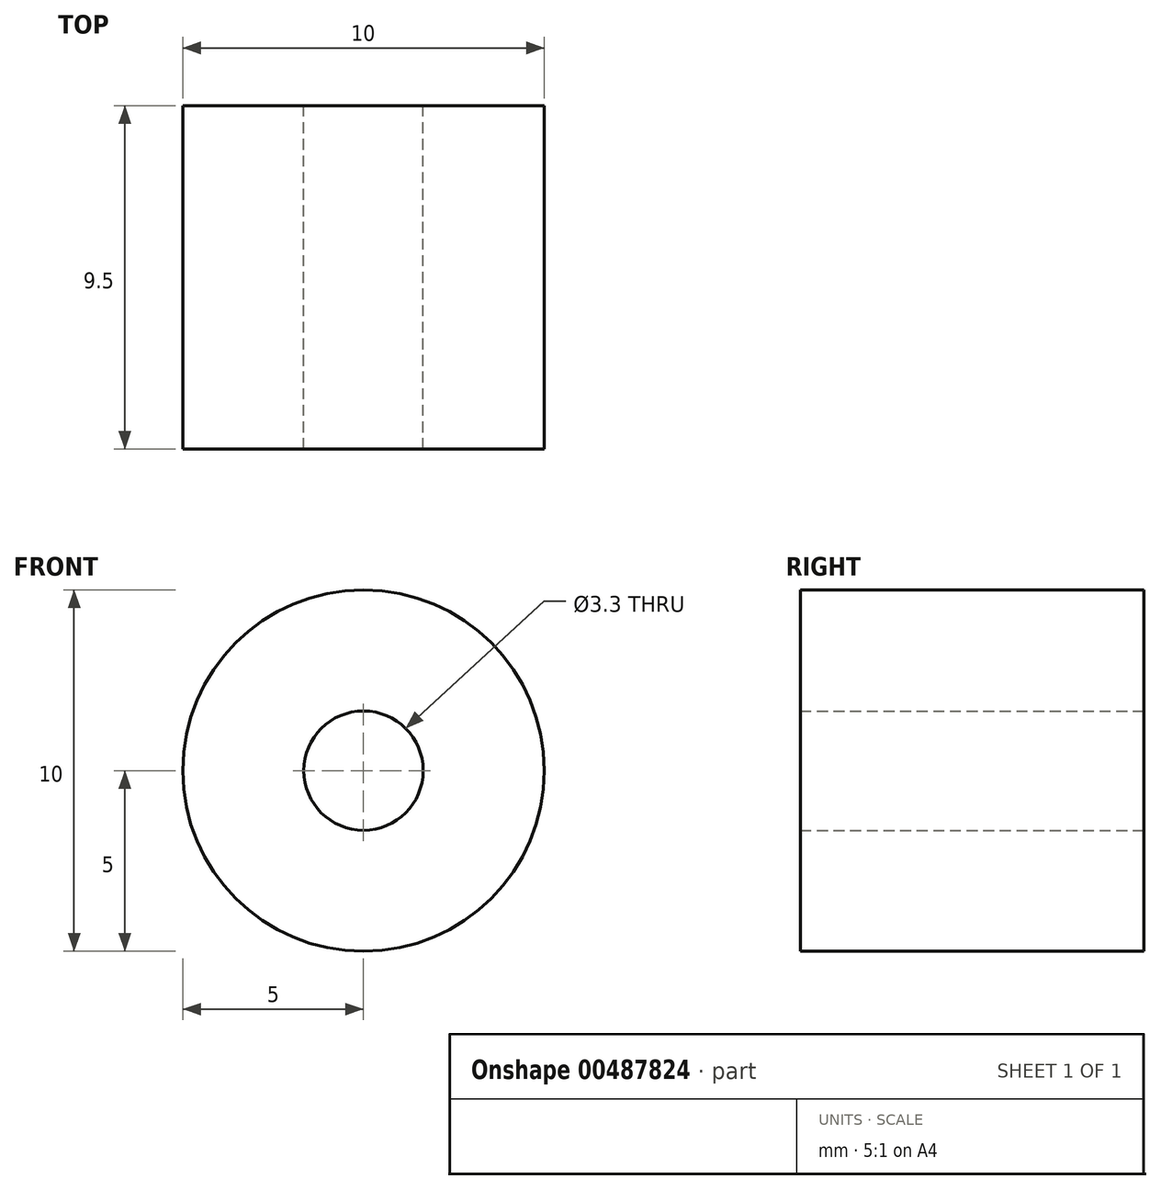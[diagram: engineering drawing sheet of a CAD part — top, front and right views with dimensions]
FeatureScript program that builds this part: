
annotation { "Feature Type Name" : "Feature", "Feature Type Description" : "" }
export const myFeature = defineFeature(function(context is Context, id is Id, definition is map)
    precondition{}
    {
        {
            var Q0;
            Q0=qCreatedBy(makeId("Front.planeOp"),FACE);
            var sketch = newSketch(context, id + "F0", { "sketchPlane" : qUnion([Q0])});
            skCircle(sketch, "E0", {"center": v(0, 0) * mm, "radius": 5 * mm});
            skCircle(sketch, "E1", {"center": v(0, 0) * mm, "radius": 1.65 * mm});
            skSolve(sketch);
        }
        {
            var Q0;
            Q0 = qSketchRegion(id + "F0", true);
            extrude(context, id + "F1", {"entities" : qUnion([Q0]), "depth" : 9.5 * mm, "offsetDistance" : 25 * mm});
        }
    });
